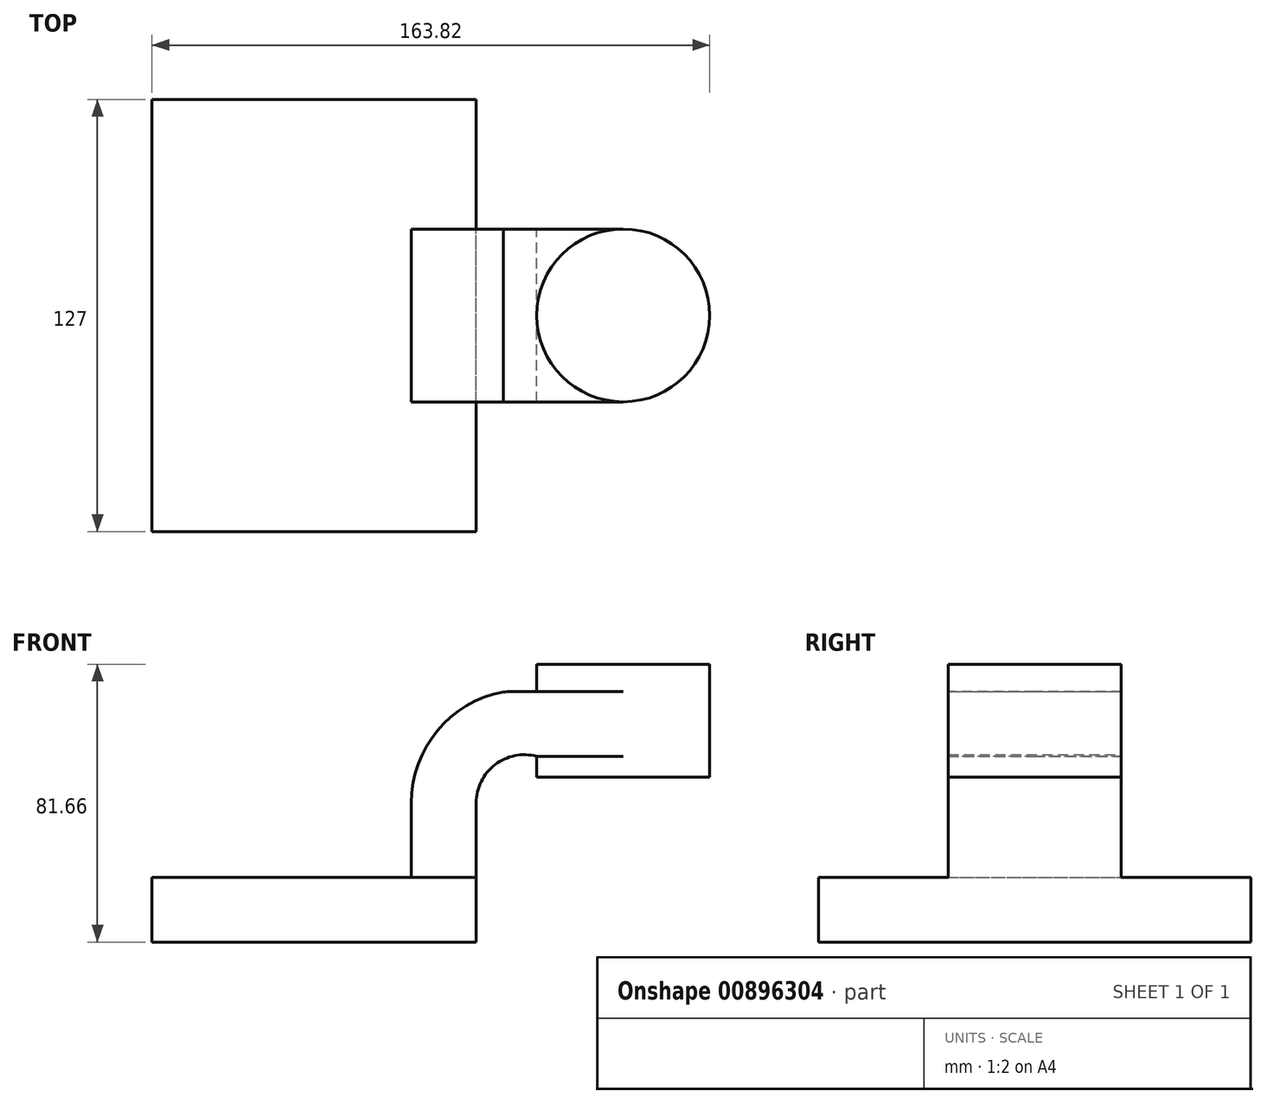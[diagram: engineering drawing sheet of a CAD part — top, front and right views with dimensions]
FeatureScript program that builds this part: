
annotation { "Feature Type Name" : "Feature", "Feature Type Description" : "" }
export const myFeature = defineFeature(function(context is Context, id is Id, definition is map)
    precondition{}
    {
        {
            var Q0;
            Q0=qCreatedBy(makeId("Front.planeOp"),FACE);
            var sketch = newSketch(context, id + "F0", { "sketchPlane" : qUnion([Q0])});
            skLineSegment(sketch, "E0.bottom", {"start": v(47.63, 9.53) * mm, "end": v(-47.63, 9.53) * mm});
            skLineSegment(sketch, "E0.top", {"start": v(47.63, -9.53) * mm, "end": v(-47.63, -9.53) * mm});
            skLineSegment(sketch, "E0.left", {"start": v(47.63, 9.53) * mm, "end": v(47.63, -9.53) * mm});
            skLineSegment(sketch, "E0.right", {"start": v(-47.63, 9.53) * mm, "end": v(-47.63, -9.53) * mm});
            skPoint(sketch, "E0.middle", {"position": v(0, 0) * mm});
            skLineSegment(sketch, "E1.bottom", {"start": v(116.2, 72.13) * mm, "end": v(65.4, 72.13) * mm});
            skLineSegment(sketch, "E1.top", {"start": v(116.2, 38.93) * mm, "end": v(65.4, 38.93) * mm});
            skLineSegment(sketch, "E1.left", {"start": v(116.2, 72.13) * mm, "end": v(116.2, 38.93) * mm});
            skLineSegment(sketch, "E1.right", {"start": v(65.4, 72.13) * mm, "end": v(65.4, 38.93) * mm});
            skPoint(sketch, "E1.middle", {"position": v(90.8, 55.53) * mm});
            skLineSegment(sketch, "E2", {"start": v(47.63, 9.53) * mm, "end": v(47.63, 31.38) * mm});
            skArc(sketch, "E3", {"start": v(47.63, 31.38) * mm, "mid": v(53.15, 42.59) * mm, "end": v(65.4, 45.05) * mm});
            skArc(sketch, "E4.1", {"start": v(28.58, 31.38) * mm, "mid": v(36.19, 52.53) * mm, "end": v(55.53, 63.98) * mm});
            skLineSegment(sketch, "E4.2", {"start": v(28.57, 9.53) * mm, "end": v(28.57, 31.38) * mm});
            skFitSpline(sketch, "E5", {"points": [v(-47.63, 9.53) * mm, v(7.04, 56.25) * mm, v(67.36, 64.1) * mm, v(69.11, 60.34) * mm], "startDerivative": vector(101.22, 119.66) * mm, "endDerivative": vector(0, -101.34) * mm});
            skPoint(sketch, "E6.end.orphan", {"position": v(90.8, 38.93) * mm});
            skLineSegment(sketch, "E7", {"start": v(65.4, 64.1) * mm, "end": v(90.8, 64.1) * mm});
            skLineSegment(sketch, "E8", {"start": v(65.4, 45.05) * mm, "end": v(90.8, 45.05) * mm});
            skLineSegment(sketch, "E9", {"start": v(90.8, 72.13) * mm, "end": v(90.8, 38.93) * mm});
            skSolve(sketch);
        }
        {
            var Q0;
            Q0=makeQuery(id+"F0.imprint","IMPRINT",FACE,{"disambiguationData":[TD([[makeQuery(id+"F0.imprint","IMPRINT",EDGE,{"derivedFrom":sQuery(id+"F0.wireOp",EDGE,"E0.top")}),-1.0]])]});
            extrude(context, id + "F1", {"entities" : qUnion([Q0]), "endBound" : BoundingType.SYMMETRIC, "depth" : 127 * mm, "offsetDistance" : 25.4 * mm});
        }
        {
            var Q0;
            {var subQ4=sQuery(id+"F0.wireOp",EDGE,"E4.1");Q0=makeQuery(id+"F0.imprint","IMPRINT",FACE,{"disambiguationData":[TD([[makeQuery(id+"F0.imprint","IMPRINT",EDGE,{"derivedFrom":subQ4}),1.0]])]});}
            extrude(context, id + "F2", {"entities" : qUnion([Q0]), "operationType" : NewBodyOperationType.ADD, "endBound" : BoundingType.SYMMETRIC, "depth" : 25.4 * mm, "offsetDistance" : 25.4 * mm});
        }
        {
            var Q0;
            {var subQ1=sQuery(id+"F0.wireOp",EDGE,"E2");Q0=makeQuery(id+"F0.imprint","IMPRINT",FACE,{"disambiguationData":[TD([[makeQuery(id+"F0.imprint","IMPRINT",EDGE,{"derivedFrom":subQ1}),1.0]])]});}
            var Q1;
            {var subQ0=sQuery(id+"F0.wireOp",EDGE,"xuZzrqjS-omZf-Xl9w-YPcI-D5J2gvV31Ueq");Q1=makeQuery(id+"F0.imprint","IMPRINT",FACE,{"disambiguationData":[TD([[makeQuery(id+"F0.imprint","IMPRINT",EDGE,{"derivedFrom":subQ0}),1.0]])]});}
            var Q2;
            {var subQ2=sQuery(id+"F0.wireOp",EDGE,"E7");Q2=makeQuery(id+"F0.imprint","IMPRINT",FACE,{"disambiguationData":[TD([[makeQuery(id+"F0.imprint","IMPRINT",EDGE,{"derivedFrom":subQ2}),-1.0]])]});}
            extrude(context, id + "F3", {"entities" : qUnion([Q0, Q1, Q2]), "operationType" : NewBodyOperationType.ADD, "endBound" : BoundingType.SYMMETRIC, "depth" : 50.8 * mm, "offsetDistance" : 25.4 * mm});
        }
        {
            var Q0;
            {var subQ4=sQuery(id+"F0.wireOp",EDGE,"E1.left");Q0=makeQuery(id+"F0.imprint","IMPRINT",FACE,{"disambiguationData":[TD([[makeQuery(id+"F0.imprint","IMPRINT",EDGE,{"derivedFrom":subQ4}),-1.0]])]});}
            var Q1;
            Q1=sQuery(id+"F0.wireOp",EDGE,"E9");
            revolve(context, id + "F4", {"operationType" : NewBodyOperationType.ADD, "surfaceOperationType" : NewSurfaceOperationType.NEW, "entities" : qUnion([Q0]), "axis" : qUnion([Q1]), "revolveType" : RevolveType.FULL});
        }
    });
